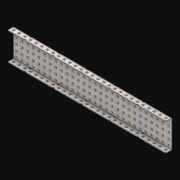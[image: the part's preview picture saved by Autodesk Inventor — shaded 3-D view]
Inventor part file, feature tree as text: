
AUTODESK INVENTOR PART (.ipt)
format: ipt  version: 2021 (Build 250183000, 183)  size: 3,705,856 bytes
history: native  units: in
note: dims shown in document units (in); Inventor stores cm internally (conversion verified against a paired STEP export)
features: extrude x197, other x196, sketch x4, thicken_offset x3, pattern_linear x3, imported_body x1
ambient origin geometry x8: Origin, YZ Plane, XZ Plane, XY Plane, X Axis, Y Axis, Z Axis, Center Point
bodies: Solid1 (feature_tree)
feature tree (404):
  thicken_offset  "Thicken1"
  thicken_offset  "Thicken2"
  thicken_offset  "Thicken3"
  pattern_linear  "Rectangular Pattern1"  Spacing1=0.001in  [1 undecoded]
  pattern_linear  "Rectangular Pattern2"  Spacing1=0.001in  [1 undecoded]
  pattern_linear  "Rectangular Pattern3"  Spacing1=0.182in  [1 undecoded]
  extrude  "Extrusion1"  Depth=0.063in TaperAngle=0.0deg
  sketch  "Sketch1"  dims[d0=0.001in]
  other  "Srf1"
  sketch  "Sketch2"  dims[d1=0.001in]
  other  "Srf2"
  sketch  "Sketch3"  dims[d2=0.001in]
  other  "Srf3"
  other  "Srf4"
  other  "Srf5"
  other  "Srf6"
  other  "Srf7"
  other  "Srf8"
  other  "Srf9"
  other  "Srf10"
  other  "Srf11"
  other  "Srf12"
  other  "Srf13"
  other  "Srf14"
  other  "Srf15"
  other  "Srf16"
  other  "Srf17"
  other  "Srf18"
  other  "Srf19"
  other  "Srf20"
  other  "Srf21"
  other  "Srf22"
  other  "Srf23"
  other  "Srf24"
  other  "Srf25"
  other  "Srf26"
  other  "Srf27"
  other  "Srf28"
  other  "Srf29"
  other  "Srf30"
  other  "Srf38"
  other  "Srf39"
  other  "Srf40"
  other  "Srf41"
  other  "Srf42"
  other  "Srf43"
  other  "Srf44"
  other  "Srf45"
  other  "Srf46"
  other  "Srf47"
  other  "Srf48"
  other  "Srf49"
  other  "Srf50"
  other  "Srf51"
  other  "Srf52"
  other  "Srf53"
  other  "Srf54"
  other  "Srf55"
  other  "Srf56"
  other  "Srf57"
  other  "Srf58"
  other  "Srf59"
  other  "Srf60"
  other  "Srf61"
  other  "Srf62"
  other  "Srf63"
  other  "Srf64"
  other  "Srf72"
  other  "Srf73"
  other  "Srf74"
  other  "Srf75"
  other  "Srf76"
  other  "Srf77"
  other  "Srf78"
  other  "Srf79"
  other  "Srf80"
  other  "Srf81"
  other  "Srf82"
  other  "Srf83"
  other  "Srf84"
  other  "Srf85"
  other  "Srf86"
  other  "Srf87"
  other  "Srf88"
  other  "Srf89"
  other  "Srf90"
  other  "Srf91"
  other  "Srf92"
  other  "Srf93"
  other  "Srf94"
  other  "Srf95"
  other  "Srf96"
  other  "Srf97"
  other  "Srf98"
  other  "Srf106"
  other  "Srf107"
  other  "Srf108"
  other  "Srf109"
  other  "Srf110"
  other  "Srf111"
  other  "Srf112"
  other  "Srf113"
  other  "Srf114"
  other  "Srf115"
  other  "Srf116"
  other  "Srf117"
  other  "Srf118"
  other  "Srf119"
  other  "Srf120"
  other  "Srf121"
  other  "Srf122"
  other  "Srf123"
  other  "Srf124"
  other  "Srf125"
  other  "Srf126"
  other  "Srf127"
  other  "Srf128"
  other  "Srf129"
  other  "Srf130"
  other  "Srf131"
  other  "Srf132"
  other  "Srf133"
  other  "Srf141"
  other  "Srf142"
  other  "Srf143"
  other  "Srf144"
  other  "Srf145"
  other  "Srf146"
  other  "Srf147"
  other  "Srf148"
  other  "Srf149"
  other  "Srf150"
  other  "Srf151"
  other  "Srf152"
  other  "Srf153"
  other  "Srf154"
  other  "Srf155"
  other  "Srf156"
  other  "Srf157"
  other  "Srf158"
  other  "Srf159"
  other  "Srf160"
  other  "Srf161"
  other  "Srf162"
  other  "Srf163"
  other  "Srf164"
  other  "Srf165"
  other  "Srf166"
  other  "Srf167"
  other  "Srf168"
  other  "Srf176"
  other  "Srf177"
  other  "Srf178"
  other  "Srf179"
  other  "Srf180"
  other  "Srf181"
  other  "Srf182"
  other  "Srf183"
  other  "Srf184"
  other  "Srf185"
  other  "Srf186"
  other  "Srf187"
  other  "Srf188"
  other  "Srf189"
  other  "Srf190"
  other  "Srf191"
  other  "Srf192"
  other  "Srf193"
  other  "Srf194"
  other  "Srf195"
  other  "Srf196"
  other  "Srf197"
  other  "Srf198"
  other  "Srf199"
  other  "Srf200"
  other  "Srf201"
  other  "Srf202"
  other  "Srf203"
  other  "Srf211"
  other  "Srf212"
  other  "Srf213"
  other  "Srf214"
  other  "Srf215"
  other  "Srf216"
  other  "Srf217"
  other  "Srf218"
  other  "Srf219"
  other  "Srf220"
  other  "Srf221"
  other  "Srf222"
  other  "Srf223"
  other  "Srf224"
  other  "Srf225"
  other  "Srf226"
  other  "Srf227"
  other  "Srf228"
  other  "Srf229"
  other  "Srf230"
  other  "Srf231"
  other  "Srf232"
  other  "Srf233"
  other  "Srf234"
  other  "Srf235"
  other  "Srf236"
  other  "Srf237"
  other  "Srf238"
  sketch  "Sketch4"  dims[d3=0.001in d4=0.001in d5=0.001in d6=0.182in d7=0.063in d8=0.0in d9=0.182in d10=0.063in d11=0.0in d12=0.182in d13=0.063in d14=0.0in d17=0.5in d18=11.0236in d20=0.5in d21=11.0236in d23=0.5in d24=1.9685in d26=0.5in d27=3.5in d28=0.0in]
  imported_body  "Imported1"
  extrude  "ExtrusionSrf1"  Depth=3.5in
  extrude  "ExtrusionSrf2"  Depth=0.063in TaperAngle=0.0deg
  extrude  "ExtrusionSrf3"  Depth=3.5in
  extrude  "ExtrusionSrf4"  Depth=0.063in TaperAngle=0.0deg
  extrude  "ExtrusionSrf5"  Depth=0.5in
  extrude  "ExtrusionSrf6"  Depth=3.5in
  extrude  "ExtrusionSrf7"  Depth=0.5in
  extrude  "ExtrusionSrf8"  Depth=3.5in
  extrude  "ExtrusionSrf9"  Depth=0.5in
  extrude  "ExtrusionSrf10"  Depth=0.5in
  extrude  "ExtrusionSrf11"  Depth=3.5in
  extrude  "ExtrusionSrf12"  TaperAngle=0.0deg  [1 undecoded]
  extrude  "ExtrusionSrf13"  [1 undecoded]
  extrude  "ExtrusionSrf14"  [1 undecoded]
  extrude  "ExtrusionSrf15"  [1 undecoded]
  extrude  "ExtrusionSrf16"  [1 undecoded]
  extrude  "ExtrusionSrf17"  [1 undecoded]
  extrude  "ExtrusionSrf18"  [1 undecoded]
  extrude  "ExtrusionSrf19"  [1 undecoded]
  extrude  "ExtrusionSrf20"  [1 undecoded]
  extrude  "ExtrusionSrf21"  [1 undecoded]
  extrude  "ExtrusionSrf22"  [1 undecoded]
  extrude  "ExtrusionSrf23"  [1 undecoded]
  extrude  "ExtrusionSrf24"  [1 undecoded]
  extrude  "ExtrusionSrf25"  [1 undecoded]
  extrude  "ExtrusionSrf26"  [1 undecoded]
  extrude  "ExtrusionSrf27"  [1 undecoded]
  extrude  "ExtrusionSrf28"  [1 undecoded]
  extrude  "ExtrusionSrf29"  [1 undecoded]
  extrude  "ExtrusionSrf30"  [1 undecoded]
  extrude  "ExtrusionSrf38"  [1 undecoded]
  extrude  "ExtrusionSrf39"  [1 undecoded]
  extrude  "ExtrusionSrf40"  [1 undecoded]
  extrude  "ExtrusionSrf41"  [1 undecoded]
  extrude  "ExtrusionSrf42"  [1 undecoded]
  extrude  "ExtrusionSrf43"  [1 undecoded]
  extrude  "ExtrusionSrf44"  [1 undecoded]
  extrude  "ExtrusionSrf45"  [1 undecoded]
  extrude  "ExtrusionSrf46"  [1 undecoded]
  extrude  "ExtrusionSrf47"  [1 undecoded]
  extrude  "ExtrusionSrf48"  [1 undecoded]
  extrude  "ExtrusionSrf49"  [1 undecoded]
  extrude  "ExtrusionSrf50"  [1 undecoded]
  extrude  "ExtrusionSrf51"  [1 undecoded]
  extrude  "ExtrusionSrf52"  [1 undecoded]
  extrude  "ExtrusionSrf53"  [1 undecoded]
  extrude  "ExtrusionSrf54"  [1 undecoded]
  extrude  "ExtrusionSrf55"  [1 undecoded]
  extrude  "ExtrusionSrf56"  [1 undecoded]
  extrude  "ExtrusionSrf57"  [1 undecoded]
  extrude  "ExtrusionSrf58"  [1 undecoded]
  extrude  "ExtrusionSrf59"  [1 undecoded]
  extrude  "ExtrusionSrf60"  [1 undecoded]
  extrude  "ExtrusionSrf61"  [1 undecoded]
  extrude  "ExtrusionSrf62"  [1 undecoded]
  extrude  "ExtrusionSrf63"  [1 undecoded]
  extrude  "ExtrusionSrf64"  [1 undecoded]
  extrude  "ExtrusionSrf72"  [1 undecoded]
  extrude  "ExtrusionSrf73"  [1 undecoded]
  extrude  "ExtrusionSrf74"  [1 undecoded]
  extrude  "ExtrusionSrf75"  [1 undecoded]
  extrude  "ExtrusionSrf76"  [1 undecoded]
  extrude  "ExtrusionSrf77"  [1 undecoded]
  extrude  "ExtrusionSrf78"  [1 undecoded]
  extrude  "ExtrusionSrf79"  [1 undecoded]
  extrude  "ExtrusionSrf80"  [1 undecoded]
  extrude  "ExtrusionSrf81"  [1 undecoded]
  extrude  "ExtrusionSrf82"  [1 undecoded]
  extrude  "ExtrusionSrf83"  [1 undecoded]
  extrude  "ExtrusionSrf84"  [1 undecoded]
  extrude  "ExtrusionSrf85"  [1 undecoded]
  extrude  "ExtrusionSrf86"  [1 undecoded]
  extrude  "ExtrusionSrf87"  [1 undecoded]
  extrude  "ExtrusionSrf88"  [1 undecoded]
  extrude  "ExtrusionSrf89"  [1 undecoded]
  extrude  "ExtrusionSrf90"  [1 undecoded]
  extrude  "ExtrusionSrf91"  [1 undecoded]
  extrude  "ExtrusionSrf92"  [1 undecoded]
  extrude  "ExtrusionSrf93"  [1 undecoded]
  extrude  "ExtrusionSrf94"  [1 undecoded]
  extrude  "ExtrusionSrf95"  [1 undecoded]
  extrude  "ExtrusionSrf96"  [1 undecoded]
  extrude  "ExtrusionSrf97"  [1 undecoded]
  extrude  "ExtrusionSrf98"  [1 undecoded]
  extrude  "ExtrusionSrf106"  [1 undecoded]
  extrude  "ExtrusionSrf107"  [1 undecoded]
  extrude  "ExtrusionSrf108"  [1 undecoded]
  extrude  "ExtrusionSrf109"  [1 undecoded]
  extrude  "ExtrusionSrf110"  [1 undecoded]
  extrude  "ExtrusionSrf111"  [1 undecoded]
  extrude  "ExtrusionSrf112"  [1 undecoded]
  extrude  "ExtrusionSrf113"  [1 undecoded]
  extrude  "ExtrusionSrf114"  [1 undecoded]
  extrude  "ExtrusionSrf115"  [1 undecoded]
  extrude  "ExtrusionSrf116"  [1 undecoded]
  extrude  "ExtrusionSrf117"  [1 undecoded]
  extrude  "ExtrusionSrf118"  [1 undecoded]
  extrude  "ExtrusionSrf119"  [1 undecoded]
  extrude  "ExtrusionSrf120"  [1 undecoded]
  extrude  "ExtrusionSrf121"  [1 undecoded]
  extrude  "ExtrusionSrf122"  [1 undecoded]
  extrude  "ExtrusionSrf123"  [1 undecoded]
  extrude  "ExtrusionSrf124"  [1 undecoded]
  extrude  "ExtrusionSrf125"  [1 undecoded]
  extrude  "ExtrusionSrf126"  [1 undecoded]
  extrude  "ExtrusionSrf127"  [1 undecoded]
  extrude  "ExtrusionSrf128"  [1 undecoded]
  extrude  "ExtrusionSrf129"  [1 undecoded]
  extrude  "ExtrusionSrf130"  [1 undecoded]
  extrude  "ExtrusionSrf131"  [1 undecoded]
  extrude  "ExtrusionSrf132"  [1 undecoded]
  extrude  "ExtrusionSrf133"  [1 undecoded]
  extrude  "ExtrusionSrf141"  [1 undecoded]
  extrude  "ExtrusionSrf142"  [1 undecoded]
  extrude  "ExtrusionSrf143"  [1 undecoded]
  extrude  "ExtrusionSrf144"  [1 undecoded]
  extrude  "ExtrusionSrf145"  [1 undecoded]
  extrude  "ExtrusionSrf146"  [1 undecoded]
  extrude  "ExtrusionSrf147"  [1 undecoded]
  extrude  "ExtrusionSrf148"  [1 undecoded]
  extrude  "ExtrusionSrf149"  [1 undecoded]
  extrude  "ExtrusionSrf150"  [1 undecoded]
  extrude  "ExtrusionSrf151"  [1 undecoded]
  extrude  "ExtrusionSrf152"  [1 undecoded]
  extrude  "ExtrusionSrf153"  [1 undecoded]
  extrude  "ExtrusionSrf154"  [1 undecoded]
  extrude  "ExtrusionSrf155"  [1 undecoded]
  extrude  "ExtrusionSrf156"  [1 undecoded]
  extrude  "ExtrusionSrf157"  [1 undecoded]
  extrude  "ExtrusionSrf158"  [1 undecoded]
  extrude  "ExtrusionSrf159"  [1 undecoded]
  extrude  "ExtrusionSrf160"  [1 undecoded]
  extrude  "ExtrusionSrf161"  [1 undecoded]
  extrude  "ExtrusionSrf162"  [1 undecoded]
  extrude  "ExtrusionSrf163"  [1 undecoded]
  extrude  "ExtrusionSrf164"  [1 undecoded]
  extrude  "ExtrusionSrf165"  [1 undecoded]
  extrude  "ExtrusionSrf166"  [1 undecoded]
  extrude  "ExtrusionSrf167"  [1 undecoded]
  extrude  "ExtrusionSrf168"  [1 undecoded]
  extrude  "ExtrusionSrf176"  [1 undecoded]
  extrude  "ExtrusionSrf177"  [1 undecoded]
  extrude  "ExtrusionSrf178"  [1 undecoded]
  extrude  "ExtrusionSrf179"  [1 undecoded]
  extrude  "ExtrusionSrf180"  [1 undecoded]
  extrude  "ExtrusionSrf181"  [1 undecoded]
  extrude  "ExtrusionSrf182"  [1 undecoded]
  extrude  "ExtrusionSrf183"  [1 undecoded]
  extrude  "ExtrusionSrf184"  [1 undecoded]
  extrude  "ExtrusionSrf185"  [1 undecoded]
  extrude  "ExtrusionSrf186"  [1 undecoded]
  extrude  "ExtrusionSrf187"  [1 undecoded]
  extrude  "ExtrusionSrf188"  [1 undecoded]
  extrude  "ExtrusionSrf189"  [1 undecoded]
  extrude  "ExtrusionSrf190"  [1 undecoded]
  extrude  "ExtrusionSrf191"  [1 undecoded]
  extrude  "ExtrusionSrf192"  [1 undecoded]
  extrude  "ExtrusionSrf193"  [1 undecoded]
  extrude  "ExtrusionSrf194"  [1 undecoded]
  extrude  "ExtrusionSrf195"  [1 undecoded]
  extrude  "ExtrusionSrf196"  [1 undecoded]
  extrude  "ExtrusionSrf197"  [1 undecoded]
  extrude  "ExtrusionSrf198"  [1 undecoded]
  extrude  "ExtrusionSrf199"  [1 undecoded]
  extrude  "ExtrusionSrf200"  [1 undecoded]
  extrude  "ExtrusionSrf201"  [1 undecoded]
  extrude  "ExtrusionSrf202"  [1 undecoded]
  extrude  "ExtrusionSrf203"  [1 undecoded]
  extrude  "ExtrusionSrf211"  [1 undecoded]
  extrude  "ExtrusionSrf212"  [1 undecoded]
  extrude  "ExtrusionSrf213"  [1 undecoded]
  extrude  "ExtrusionSrf214"  [1 undecoded]
  extrude  "ExtrusionSrf215"  [1 undecoded]
  extrude  "ExtrusionSrf216"  [1 undecoded]
  extrude  "ExtrusionSrf217"  [1 undecoded]
  extrude  "ExtrusionSrf218"  [1 undecoded]
  extrude  "ExtrusionSrf219"  [1 undecoded]
  extrude  "ExtrusionSrf220"  [1 undecoded]
  extrude  "ExtrusionSrf221"  [1 undecoded]
  extrude  "ExtrusionSrf222"  [1 undecoded]
  extrude  "ExtrusionSrf223"  [1 undecoded]
  extrude  "ExtrusionSrf224"  [1 undecoded]
  extrude  "ExtrusionSrf225"  [1 undecoded]
  extrude  "ExtrusionSrf226"  [1 undecoded]
  extrude  "ExtrusionSrf227"  [1 undecoded]
  extrude  "ExtrusionSrf228"  [1 undecoded]
  extrude  "ExtrusionSrf229"  [1 undecoded]
  extrude  "ExtrusionSrf230"  [1 undecoded]
  extrude  "ExtrusionSrf231"  [1 undecoded]
  extrude  "ExtrusionSrf232"  [1 undecoded]
  extrude  "ExtrusionSrf233"  [1 undecoded]
  extrude  "ExtrusionSrf234"  [1 undecoded]
  extrude  "ExtrusionSrf235"  [1 undecoded]
  extrude  "ExtrusionSrf236"  [1 undecoded]
  extrude  "ExtrusionSrf237"  [1 undecoded]
  extrude  "ExtrusionSrf238"  [1 undecoded]
note: 188 required parameter values undecoded (feature->parameter linkage not recoverable at this tier; creation-order binding heuristic only, values carry confidence <= 0.55)
